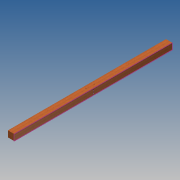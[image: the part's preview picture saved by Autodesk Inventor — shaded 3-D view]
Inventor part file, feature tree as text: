
AUTODESK INVENTOR PART (.ipt)
format: ipt  version: 2014 SP1 (Build 180222100, 222)  size: 90,624 bytes
history: native  units: in
note: dims shown in document units (in); Inventor stores cm internally (conversion verified against a paired STEP export)
features: sketch x3, extrude x1, hole x1
ambient origin geometry x8: Origin, YZ Plane, XZ Plane, XY Plane, X Axis, Y Axis, Z Axis, Center Point
bodies: Solid1 (feature_tree)
feature tree (5):
  extrude  "Extrusion1"  Depth=1.5in
  hole  "Hole2"  [1 undecoded]
  sketch  "Sketch4"  dims[d22=0.201in d23=0.75in d24=0.385in d25=0.25in d26=0.5635in d27=1.0in d28=0.8108in]
  sketch  "Sketch1"  dims[d0=1.5in d1=1.5in]
  sketch  "Sketch3"  dims[d2=39.0in d3=0.0in d21=1.0in]
note: 1 required parameter value undecoded (feature->parameter linkage not recoverable at this tier; creation-order binding heuristic only, values carry confidence <= 0.55)
